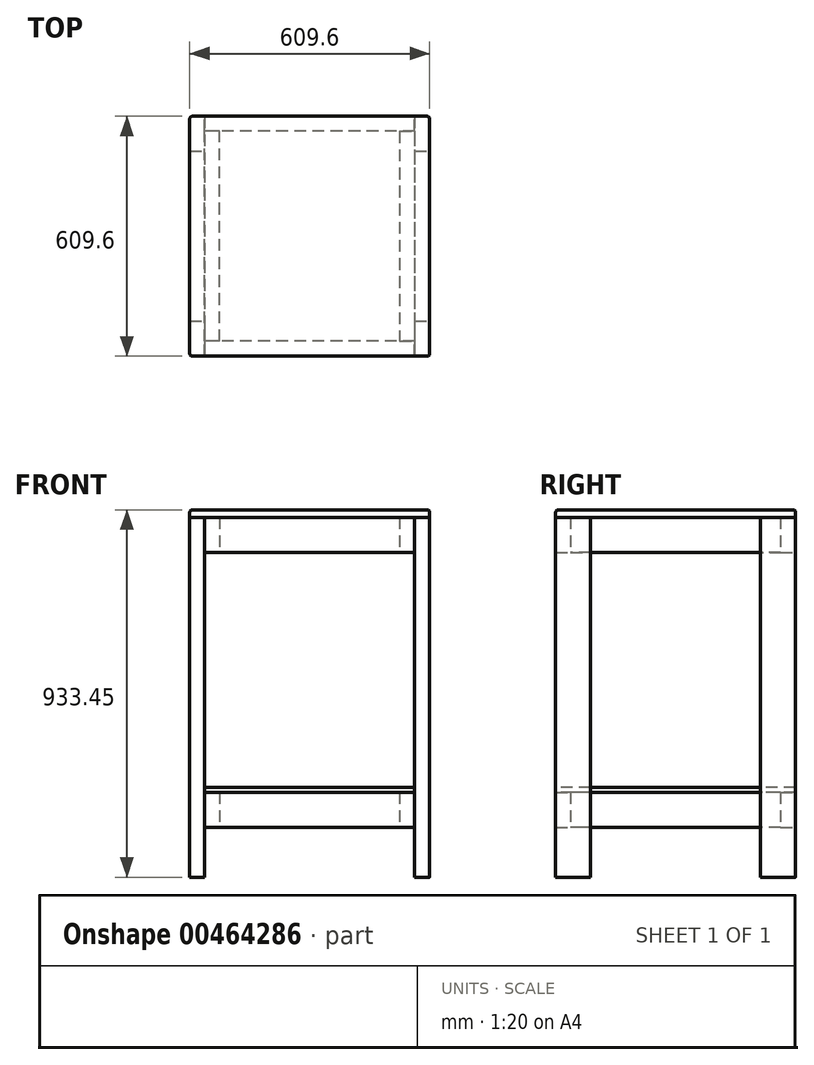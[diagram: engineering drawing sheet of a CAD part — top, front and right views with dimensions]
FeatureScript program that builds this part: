
annotation { "Feature Type Name" : "Feature", "Feature Type Description" : "" }
export const myFeature = defineFeature(function(context is Context, id is Id, definition is map)
    precondition{}
    {
        {
            var Q0;
            Q0=qCreatedBy(makeId("Top.planeOp"),FACE);
            var sketch = newSketch(context, id + "F0", { "sketchPlane" : qUnion([Q0])});
            skLineSegment(sketch, "E0.bottom", {"start": v(571.5, 0) * mm, "end": v(609.6, 0) * mm});
            skLineSegment(sketch, "E0.top", {"start": v(571.5, -88.9) * mm, "end": v(609.6, -88.9) * mm});
            skLineSegment(sketch, "E0.left", {"start": v(571.5, 0) * mm, "end": v(571.5, -88.9) * mm});
            skLineSegment(sketch, "E0.right", {"start": v(609.6, 0) * mm, "end": v(609.6, -88.9) * mm});
            skLineSegment(sketch, "E1.bottom", {"start": v(0, 0) * mm, "end": v(38.1, 0) * mm});
            skLineSegment(sketch, "E1.top", {"start": v(0, -88.9) * mm, "end": v(38.1, -88.9) * mm});
            skLineSegment(sketch, "E1.left", {"start": v(0, 0) * mm, "end": v(0, -88.9) * mm});
            skLineSegment(sketch, "E1.right", {"start": v(38.1, 0) * mm, "end": v(38.1, -88.9) * mm});
            skLineSegment(sketch, "E2.bottom", {"start": v(571.5, -520.7) * mm, "end": v(609.6, -520.7) * mm});
            skLineSegment(sketch, "E2.top", {"start": v(571.5, -609.6) * mm, "end": v(609.6, -609.6) * mm});
            skLineSegment(sketch, "E2.left", {"start": v(571.5, -520.7) * mm, "end": v(571.5, -609.6) * mm});
            skLineSegment(sketch, "E2.right", {"start": v(609.6, -520.7) * mm, "end": v(609.6, -609.6) * mm});
            skLineSegment(sketch, "E3.bottom", {"start": v(0, -520.7) * mm, "end": v(38.1, -520.7) * mm});
            skLineSegment(sketch, "E3.top", {"start": v(0, -609.6) * mm, "end": v(38.1, -609.6) * mm});
            skLineSegment(sketch, "E3.left", {"start": v(0, -520.7) * mm, "end": v(0, -609.6) * mm});
            skLineSegment(sketch, "E3.right", {"start": v(38.1, -520.7) * mm, "end": v(38.1, -609.6) * mm});
            skSolve(sketch);
        }
        {
            var Q0;
            Q0 = qSketchRegion(id + "F0", true);
            extrude(context, id + "F1", {"entities" : qUnion([Q0]), "depth" : 914.4 * mm});
        }
        {
            var Q0;
            Q0=makeQuery(id+"F1.opExtrude","SWEPT_FACE",FACE,{"disambiguationData":[OSD([sQuery(id+"F0.wireOp",EDGE,"E3.right")])]});
            var sketch = newSketch(context, id + "F2", { "sketchPlane" : qUnion([Q0])});
            skLineSegment(sketch, "E4.bottom", {"start": v(-609.6, 914.4) * mm, "end": v(-571.5, 914.4) * mm});
            skLineSegment(sketch, "E4.top", {"start": v(-609.6, 825.5) * mm, "end": v(-571.5, 825.5) * mm});
            skLineSegment(sketch, "E4.left", {"start": v(-609.6, 914.4) * mm, "end": v(-609.6, 825.5) * mm});
            skLineSegment(sketch, "E4.right", {"start": v(-571.5, 914.4) * mm, "end": v(-571.5, 825.5) * mm});
            skLineSegment(sketch, "E5.bottom", {"start": v(-571.5, 914.4) * mm, "end": v(-38.1, 914.4) * mm});
            skLineSegment(sketch, "E5.top", {"start": v(-571.5, 825.5) * mm, "end": v(-38.1, 825.5) * mm});
            skLineSegment(sketch, "E5.right", {"start": v(-38.1, 914.4) * mm, "end": v(-38.1, 825.5) * mm});
            skLineSegment(sketch, "E6.bottom", {"start": v(-38.1, 914.4) * mm, "end": v(0, 914.4) * mm});
            skLineSegment(sketch, "E6.top", {"start": v(-38.1, 825.5) * mm, "end": v(0, 825.5) * mm});
            skLineSegment(sketch, "E6.right", {"start": v(0, 914.4) * mm, "end": v(0, 825.5) * mm});
            skLineSegment(sketch, "E7.bottom", {"start": v(-609.6, 215.9) * mm, "end": v(-571.5, 215.9) * mm});
            skLineSegment(sketch, "E7.top", {"start": v(-609.6, 127) * mm, "end": v(-571.5, 127) * mm});
            skLineSegment(sketch, "E7.left", {"start": v(-609.6, 215.9) * mm, "end": v(-609.6, 127) * mm});
            skLineSegment(sketch, "E7.right", {"start": v(-571.5, 215.9) * mm, "end": v(-571.5, 127) * mm});
            skLineSegment(sketch, "E8.bottom", {"start": v(-571.5, 215.9) * mm, "end": v(-38.1, 215.9) * mm});
            skLineSegment(sketch, "E8.top", {"start": v(-571.5, 127) * mm, "end": v(-38.1, 127) * mm});
            skLineSegment(sketch, "E8.right", {"start": v(-38.1, 215.9) * mm, "end": v(-38.1, 127) * mm});
            skLineSegment(sketch, "E9.bottom", {"start": v(-38.1, 215.9) * mm, "end": v(0, 215.9) * mm});
            skLineSegment(sketch, "E9.top", {"start": v(-38.1, 127) * mm, "end": v(0, 127) * mm});
            skLineSegment(sketch, "E9.right", {"start": v(0, 215.9) * mm, "end": v(0, 127) * mm});
            skSolve(sketch);
        }
        {
            var Q0;
            Q0=makeQuery(id+"F2.imprint","IMPRINT",FACE,{"disambiguationData":[TD([[makeQuery(id+"F2.imprint","IMPRINT",EDGE,{"derivedFrom":sQuery(id+"F2.wireOp",EDGE,"E4.bottom")}),1.0]])]});
            var Q1;
            Q1=makeQuery(id+"F2.imprint","IMPRINT",FACE,{"disambiguationData":[TD([[makeQuery(id+"F2.imprint","IMPRINT",EDGE,{"derivedFrom":sQuery(id+"F2.wireOp",EDGE,"E9.bottom")}),-1.0]])]});
            var Q2;
            Q2=makeQuery(id+"F2.imprint","IMPRINT",FACE,{"disambiguationData":[TD([[makeQuery(id+"F2.imprint","IMPRINT",EDGE,{"derivedFrom":sQuery(id+"F2.wireOp",EDGE,"E6.bottom")}),-1.0]])]});
            var Q3;
            Q3=makeQuery(id+"F2.imprint","IMPRINT",FACE,{"disambiguationData":[TD([[makeQuery(id+"F2.imprint","IMPRINT",EDGE,{"derivedFrom":sQuery(id+"F2.wireOp",EDGE,"E7.bottom")}),-1.0]])]});
            var Q4;
            Q4=makeQuery(id+"F1.opExtrude","SWEPT_FACE",FACE,{"disambiguationData":[OSD([sQuery(id+"F0.wireOp",EDGE,"E0.left")])]});
            var Q5;
            Q5=makeQuery(id+"F1.opExtrude","SWEPT_BODY",BODY,{"disambiguationData":[OSD([sQuery(id+"F0.wireOp",EDGE,"E0.bottom"),sQuery(id+"F0.wireOp",EDGE,"E0.top"),sQuery(id+"F0.wireOp",EDGE,"E0.left"),sQuery(id+"F0.wireOp",EDGE,"E0.right")])]});
            extrude(context, id + "F3", {"entities" : qUnion([Q0, Q1, Q2, Q3]), "endBound" : BoundingType.UP_TO_SURFACE, "endBoundEntityFace" : qUnion([Q4]), "endBoundEntityBody" : qUnion([Q5]), "depth" : 265.87 * mm});
        }
        {
            var Q0;
            {var subQ3=sQuery(id+"F2.wireOp",EDGE,"E5.right");Q0=makeQuery(id+"F2.imprint","IMPRINT",FACE,{"disambiguationData":[TD([[makeQuery(id+"F2.imprint","IMPRINT",EDGE,{"derivedFrom":subQ3}),-1.0]])]});}
            var Q1;
            {var subQ0=sQuery(id+"F2.wireOp",EDGE,"E8.right");Q1=makeQuery(id+"F2.imprint","IMPRINT",FACE,{"disambiguationData":[TD([[makeQuery(id+"F2.imprint","IMPRINT",EDGE,{"derivedFrom":subQ0}),-1.0]])]});}
            var Q2;
            {var subQ0=sQuery(id+"F2.wireOp",EDGE,"E7.right");Q2=makeQuery(id+"F2.imprint","IMPRINT",FACE,{"disambiguationData":[TD([[makeQuery(id+"F2.imprint","IMPRINT",EDGE,{"derivedFrom":subQ0}),1.0]])]});}
            var Q3;
            {var subQ3=sQuery(id+"F2.wireOp",EDGE,"E4.right");Q3=makeQuery(id+"F2.imprint","IMPRINT",FACE,{"disambiguationData":[TD([[makeQuery(id+"F2.imprint","IMPRINT",EDGE,{"derivedFrom":subQ3}),1.0]])]});}
            extrude(context, id + "F4", {"entities" : qUnion([Q0, Q1, Q2, Q3]), "depth" : 38.1 * mm});
        }
        {
            var Q0;
            Q0=makeQuery(id+"F1.opExtrude","SWEPT_FACE",FACE,{"disambiguationData":[OSD([sQuery(id+"F0.wireOp",EDGE,"E0.left")])]});
            var sketch = newSketch(context, id + "F5", { "sketchPlane" : qUnion([Q0])});
            skLineSegment(sketch, "E10.bottom", {"start": v(38.1, 914.4) * mm, "end": v(571.5, 914.4) * mm});
            skLineSegment(sketch, "E10.top", {"start": v(38.1, 825.5) * mm, "end": v(571.5, 825.5) * mm});
            skLineSegment(sketch, "E10.left", {"start": v(38.1, 914.4) * mm, "end": v(38.1, 825.5) * mm});
            skLineSegment(sketch, "E10.right", {"start": v(571.5, 914.4) * mm, "end": v(571.5, 825.5) * mm});
            skLineSegment(sketch, "E11.bottom", {"start": v(38.1, 215.9) * mm, "end": v(571.5, 215.9) * mm});
            skLineSegment(sketch, "E11.top", {"start": v(38.1, 127) * mm, "end": v(571.5, 127) * mm});
            skLineSegment(sketch, "E11.left", {"start": v(38.1, 215.9) * mm, "end": v(38.1, 127) * mm});
            skLineSegment(sketch, "E11.right", {"start": v(571.5, 215.9) * mm, "end": v(571.5, 127) * mm});
            skSolve(sketch);
        }
        {
            var Q0;
            {var subQ0=sQuery(id+"F5.wireOp",EDGE,"E11.right");Q0=makeQuery(id+"F5.imprint","IMPRINT",FACE,{"disambiguationData":[TD([[makeQuery(id+"F5.imprint","IMPRINT",EDGE,{"derivedFrom":subQ0}),-1.0]])]});}
            var Q1;
            {var subQ3=sQuery(id+"F5.wireOp",EDGE,"E10.right");Q1=makeQuery(id+"F5.imprint","IMPRINT",FACE,{"disambiguationData":[TD([[makeQuery(id+"F5.imprint","IMPRINT",EDGE,{"derivedFrom":subQ3}),-1.0]])]});}
            var Q2;
            {var subQ4=sQuery(id+"F5.wireOp",EDGE,"E10.left");Q2=makeQuery(id+"F5.imprint","IMPRINT",FACE,{"disambiguationData":[TD([[makeQuery(id+"F5.imprint","IMPRINT",EDGE,{"derivedFrom":subQ4}),1.0]])]});}
            var Q3;
            {var subQ0=sQuery(id+"F5.wireOp",EDGE,"E11.left");Q3=makeQuery(id+"F5.imprint","IMPRINT",FACE,{"disambiguationData":[TD([[makeQuery(id+"F5.imprint","IMPRINT",EDGE,{"derivedFrom":subQ0}),1.0]])]});}
            extrude(context, id + "F6", {"entities" : qUnion([Q0, Q1, Q2, Q3]), "depth" : 38.1 * mm});
        }
        {
            var Q0;
            Q0=makeQuery(id+"F1.opExtrude","CAP_FACE",FACE,{"disambiguationData":[OSD([sQuery(id+"F0.wireOp",EDGE,"E0.bottom"),sQuery(id+"F0.wireOp",EDGE,"E0.top"),sQuery(id+"F0.wireOp",EDGE,"E0.left"),sQuery(id+"F0.wireOp",EDGE,"E0.right")])],"isStart":false});
            var sketch = newSketch(context, id + "F7", { "sketchPlane" : qUnion([Q0])});
            skLineSegment(sketch, "E12.bottom", {"start": v(609.6, 0) * mm, "end": v(0, 0) * mm});
            skLineSegment(sketch, "E12.top", {"start": v(609.6, -609.6) * mm, "end": v(0, -609.6) * mm});
            skLineSegment(sketch, "E12.left", {"start": v(609.6, 0) * mm, "end": v(609.6, -609.6) * mm});
            skLineSegment(sketch, "E12.right", {"start": v(0, 0) * mm, "end": v(0, -609.6) * mm});
            skSolve(sketch);
        }
        {
            var Q0;
            {var subQ4=makeQuery(id+"F1.opExtrude","CAP_EDGE",EDGE,{"disambiguationData":[OSD([sQuery(id+"F0.wireOp",EDGE,"E0.top")])],"isStart":false});Q0=makeQuery(id+"F7.imprint","IMPRINT",FACE,{"disambiguationData":[TD([[makeQuery(id+"F7.imprint","IMPRINT",EDGE,{"derivedFrom":subQ4}),1.0]])]});}
            var Q1;
            {var subQ2=sQuery(id+"F7.wireOp",EDGE,"E12.top");Q1=makeQuery(id+"F7.imprint","IMPRINT",FACE,{"disambiguationData":[TD([[makeQuery(id+"F7.imprint","IMPRINT",EDGE,{"derivedFrom":subQ2}),-1.0]])]});}
            extrude(context, id + "F8", {"entities" : qUnion([Q0, Q1]), "depth" : 19.05 * mm});
        }
        {
            var Q0;
            Q0=makeQuery(id+"F6.opExtrude","SWEPT_FACE",FACE,{"disambiguationData":[OSD([sQuery(id+"F5.wireOp",EDGE,"E11.bottom")])]});
            var sketch = newSketch(context, id + "F9", { "sketchPlane" : qUnion([Q0])});
            skLineSegment(sketch, "E13.bottom", {"start": v(571.5, 0) * mm, "end": v(38.1, 0) * mm});
            skLineSegment(sketch, "E13.top", {"start": v(571.5, -609.6) * mm, "end": v(38.1, -609.6) * mm});
            skLineSegment(sketch, "E13.left", {"start": v(571.5, 0) * mm, "end": v(571.5, -609.6) * mm});
            skLineSegment(sketch, "E13.right", {"start": v(38.1, 0) * mm, "end": v(38.1, -609.6) * mm});
            skSolve(sketch);
        }
        {
            var Q0;
            {var subQ5=sQuery(id+"F9.wireOp",EDGE,"E13.bottom");Q0=makeQuery(id+"F9.imprint","IMPRINT",FACE,{"disambiguationData":[TD([[makeQuery(id+"F9.imprint","IMPRINT",EDGE,{"derivedFrom":subQ5}),1.0]])]});}
            var Q1;
            {var subQ1=sQuery(id+"F5.wireOp",EDGE,"E11.bottom");Q1=makeQuery(id+"F9.imprint","IMPRINT",FACE,{"disambiguationData":[TD([[makeQuery(id+"F9.imprint","IMPRINT",EDGE,{"derivedFrom":makeQuery(id+"F6.opExtrude","CAP_EDGE",EDGE,{"disambiguationData":[OSD([subQ1])],"isStart":false})}),1.0]])]});}
            extrude(context, id + "F10", {"entities" : qUnion([Q0, Q1]), "depth" : 12.7 * mm});
        }
        {
            var Q0;
            Q0=makeQuery(id+"F8.opExtrude","CAP_EDGE",EDGE,{"disambiguationData":[OSD([sQuery(id+"F7.wireOp",EDGE,"E12.bottom")])],"isStart":false});
            var Q1;
            Q1=makeQuery(id+"F8.opExtrude","CAP_EDGE",EDGE,{"disambiguationData":[OSD([sQuery(id+"F7.wireOp",EDGE,"E12.left")])],"isStart":false});
            var Q2;
            Q2=makeQuery(id+"F8.opExtrude","CAP_EDGE",EDGE,{"disambiguationData":[OSD([sQuery(id+"F7.wireOp",EDGE,"E12.top")])],"isStart":false});
            var Q3;
            Q3=makeQuery(id+"F8.opExtrude","SWEPT_EDGE",EDGE,{"disambiguationData":[OSD([sQuery(id+"F7.wireOp",EDGE,"E12.bottom"),sQuery(id+"F7.wireOp",EDGE,"E12.left")])]});
            var Q4;
            Q4=makeQuery(id+"F8.opExtrude","SWEPT_EDGE",EDGE,{"disambiguationData":[OSD([sQuery(id+"F7.wireOp",EDGE,"E12.top"),sQuery(id+"F7.wireOp",EDGE,"E12.left")])]});
            var Q5;
            Q5=makeQuery(id+"F8.opExtrude","SWEPT_EDGE",EDGE,{"disambiguationData":[OSD([sQuery(id+"F7.wireOp",EDGE,"E12.top"),sQuery(id+"F7.wireOp",EDGE,"E12.right")])]});
            var Q6;
            Q6=makeQuery(id+"F8.opExtrude","CAP_EDGE",EDGE,{"disambiguationData":[OSD([sQuery(id+"F7.wireOp",EDGE,"E12.right")])],"isStart":false});
            var Q7;
            Q7=makeQuery(id+"F8.opExtrude","SWEPT_EDGE",EDGE,{"disambiguationData":[OSD([sQuery(id+"F7.wireOp",EDGE,"E12.bottom"),sQuery(id+"F7.wireOp",EDGE,"E12.right")])]});
            fillet(context, id + "F11", {"entities" : qUnion([Q0, Q1, Q2, Q3, Q4, Q5, Q6, Q7]), "radius" : 6.35 * mm, "tangentPropagation" : true, "allowEdgeOverflow" : false});
        }
        {
            var Q0;
            Q0=makeQuery(id+"F1.opExtrude","SWEPT_EDGE",EDGE,{"disambiguationData":[OSD([sQuery(id+"F0.wireOp",EDGE,"E3.top"),sQuery(id+"F0.wireOp",EDGE,"E3.left")])]});
            var Q1;
            Q1=makeQuery(id+"F1.opExtrude","SWEPT_EDGE",EDGE,{"disambiguationData":[OSD([sQuery(id+"F0.wireOp",EDGE,"E2.top"),sQuery(id+"F0.wireOp",EDGE,"E2.right")])]});
            var Q2;
            Q2=makeQuery(id+"F1.opExtrude","SWEPT_EDGE",EDGE,{"disambiguationData":[OSD([sQuery(id+"F0.wireOp",EDGE,"E0.bottom"),sQuery(id+"F0.wireOp",EDGE,"E0.right")])]});
            var Q3;
            Q3=makeQuery(id+"F1.opExtrude","SWEPT_EDGE",EDGE,{"disambiguationData":[OSD([sQuery(id+"F0.wireOp",EDGE,"E1.bottom"),sQuery(id+"F0.wireOp",EDGE,"E1.left")])]});
            fillet(context, id + "F12", {"entities" : qUnion([Q0, Q1, Q2, Q3]), "radius" : 6.35 * mm, "allowEdgeOverflow" : false});
        }
    });
